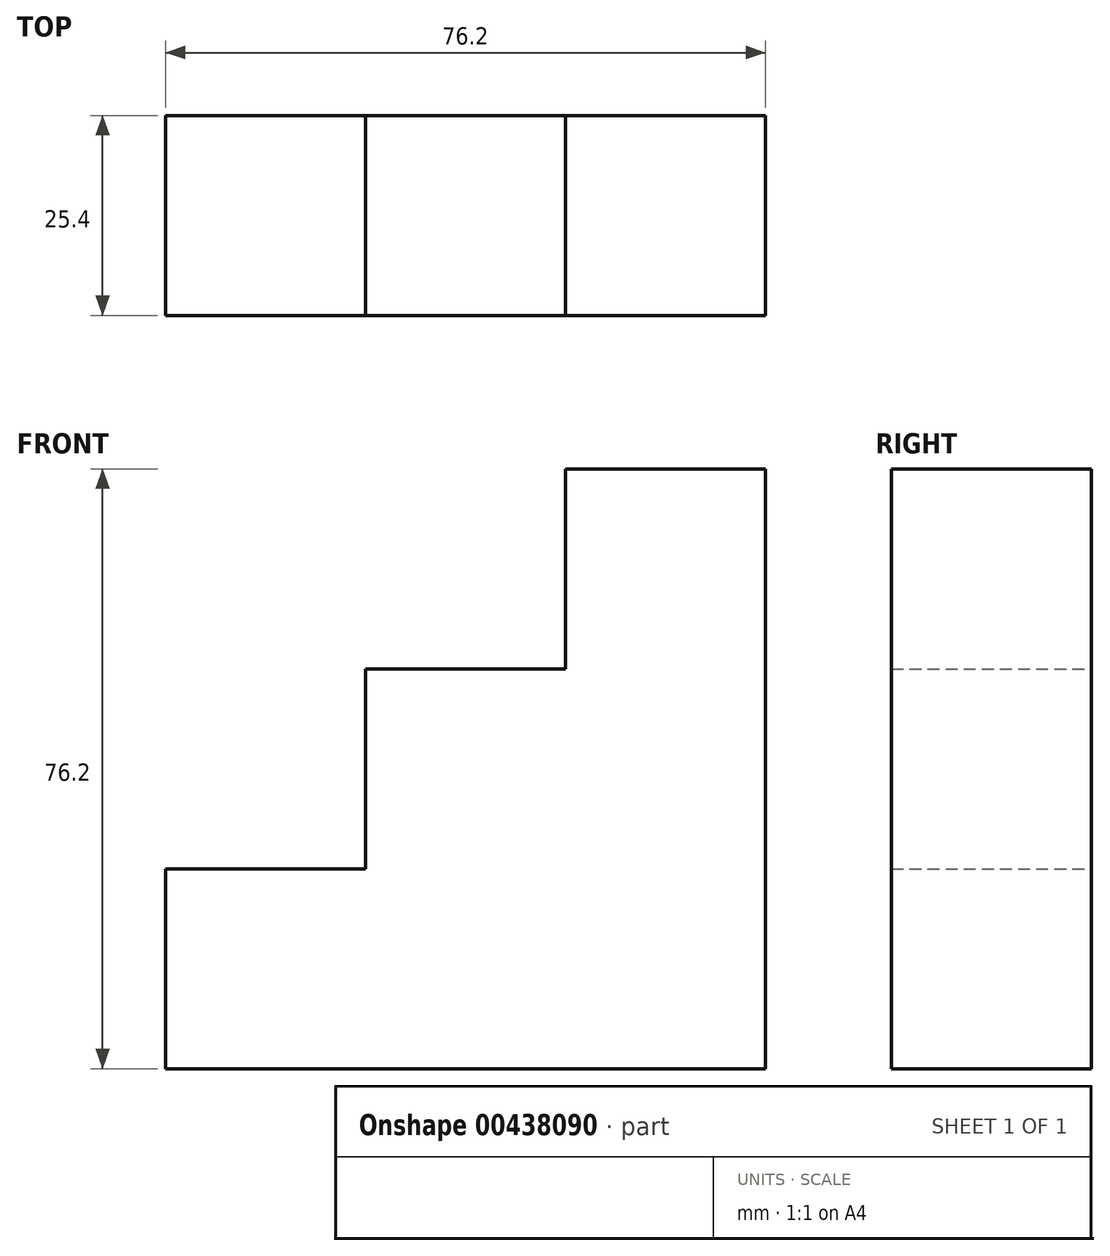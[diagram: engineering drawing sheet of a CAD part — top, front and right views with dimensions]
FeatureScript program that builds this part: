
annotation { "Feature Type Name" : "Feature", "Feature Type Description" : "" }
export const myFeature = defineFeature(function(context is Context, id is Id, definition is map)
    precondition{}
    {
        {
            var Q0;
            Q0=qCreatedBy(makeId("Front.planeOp"),FACE);
            var sketch = newSketch(context, id + "F0", { "sketchPlane" : qUnion([Q0])});
            skLineSegment(sketch, "E0", {"start": v(45.5, 59.19) * mm, "end": v(20.1, 59.19) * mm});
            skLineSegment(sketch, "E1", {"start": v(20.1, 59.19) * mm, "end": v(20.1, 33.79) * mm});
            skLineSegment(sketch, "E2", {"start": v(20.1, 33.79) * mm, "end": v(-5.3, 33.79) * mm});
            skLineSegment(sketch, "E3", {"start": v(-5.3, 33.79) * mm, "end": v(-5.3, 8.39) * mm});
            skLineSegment(sketch, "E4", {"start": v(-5.3, 8.39) * mm, "end": v(-30.7, 8.39) * mm});
            skLineSegment(sketch, "E5", {"start": v(-30.7, 8.39) * mm, "end": v(-30.7, -17.01) * mm});
            skLineSegment(sketch, "E6", {"start": v(-30.7, -17.01) * mm, "end": v(45.5, -17.01) * mm});
            skLineSegment(sketch, "E7", {"start": v(45.5, -17.01) * mm, "end": v(45.5, 59.19) * mm});
            skSolve(sketch);
        }
        {
            var Q0;
            Q0=makeQuery(id+"F0.imprint","IMPRINT",FACE,{"disambiguationData":[TD([[makeQuery(id+"F0.imprint","IMPRINT",EDGE,{"derivedFrom":sQuery(id+"F0.wireOp",EDGE,"E0")}),1.0]])]});
            extrude(context, id + "F1", {"entities" : qUnion([Q0]), "depth" : 25.4 * mm});
        }
    });
